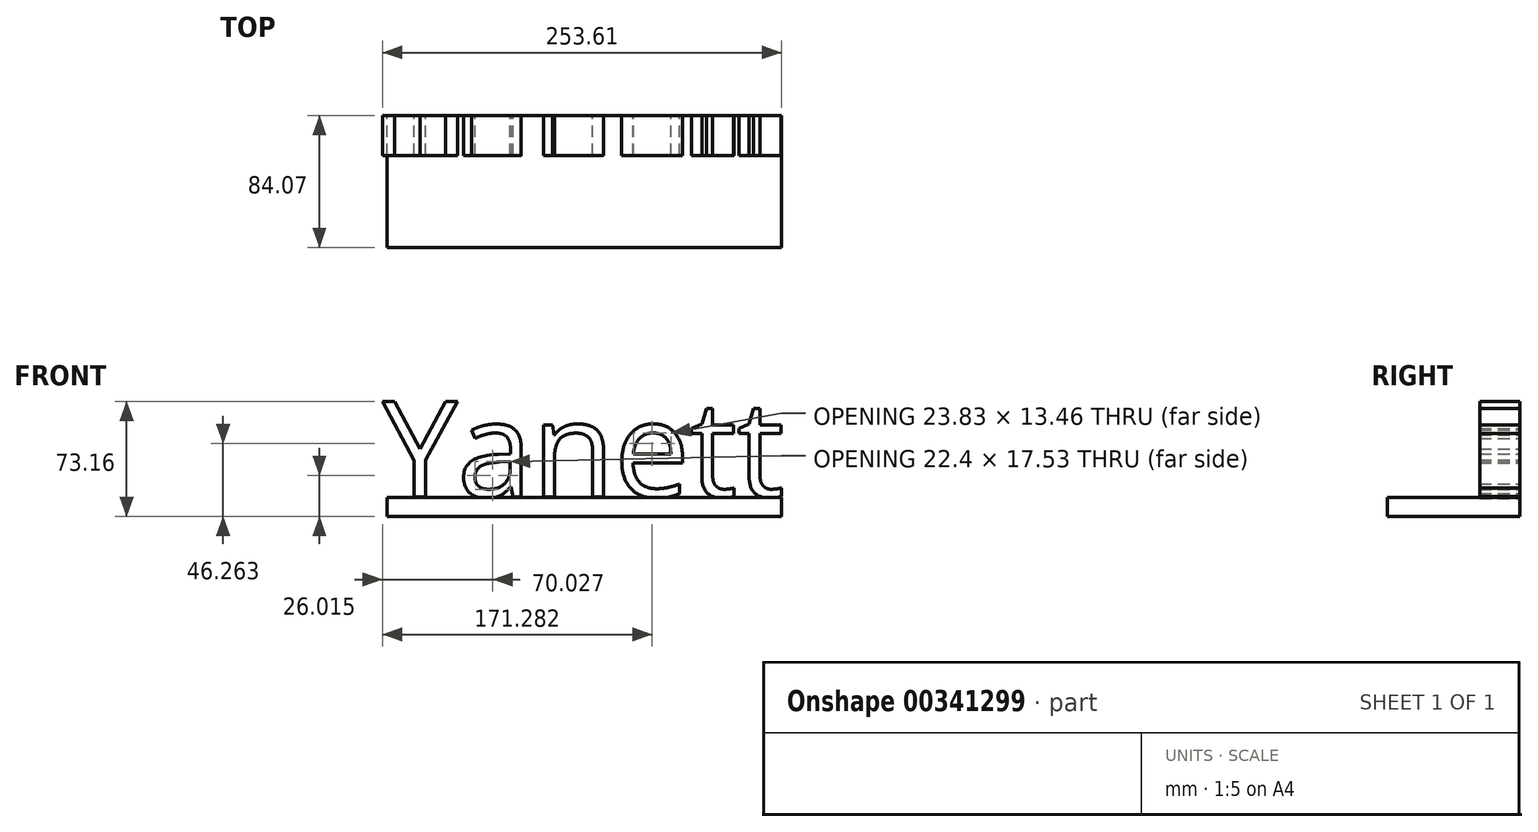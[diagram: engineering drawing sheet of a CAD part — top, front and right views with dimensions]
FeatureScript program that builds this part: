
annotation { "Feature Type Name" : "Feature", "Feature Type Description" : "" }
export const myFeature = defineFeature(function(context is Context, id is Id, definition is map)
    precondition{}
    {
        {
            var Q0;
            Q0=qCreatedBy(makeId("Front.planeOp"),FACE);
            var sketch = newSketch(context, id + "F0", { "sketchPlane" : qUnion([Q0])});
            skText(sketch, "E0", { "text": "Yanett", "fontName": "OpenSans-Regular.ttf"});
            const initialGuessF0  = {"E0": [-0.12333, -0.0236, 1, 0, 0.0613]};
            skSetInitialGuess(sketch, initialGuessF0);
            skSolve(sketch);
        }
        {
            var Q0;
            Q0 = qSketchRegion(id + "F0", true);
            extrude(context, id + "F1", {"entities" : qUnion([Q0]), "depth" : 25.4 * mm});
        }
        {
            var Q0;
            Q0=qCreatedBy(makeId("Front.planeOp"),FACE);
            var sketch = newSketch(context, id + "F2", { "sketchPlane" : qUnion([Q0])});
            skLineSegment(sketch, "E1.bottom", {"start": v(130.28, -23.89) * mm, "end": v(-120.4, -23.89) * mm});
            skLineSegment(sketch, "E1.top", {"start": v(130.28, -35.98) * mm, "end": v(-120.4, -35.98) * mm});
            skLineSegment(sketch, "E1.left", {"start": v(130.28, -23.89) * mm, "end": v(130.28, -35.98) * mm});
            skLineSegment(sketch, "E1.right", {"start": v(-120.4, -23.89) * mm, "end": v(-120.4, -35.98) * mm});
            skSolve(sketch);
        }
        {
            var Q0;
            Q0 = qSketchRegion(id + "F2", true);
            extrude(context, id + "F3", {"entities" : qUnion([Q0]), "depth" : 84.07 * mm});
        }
    });
